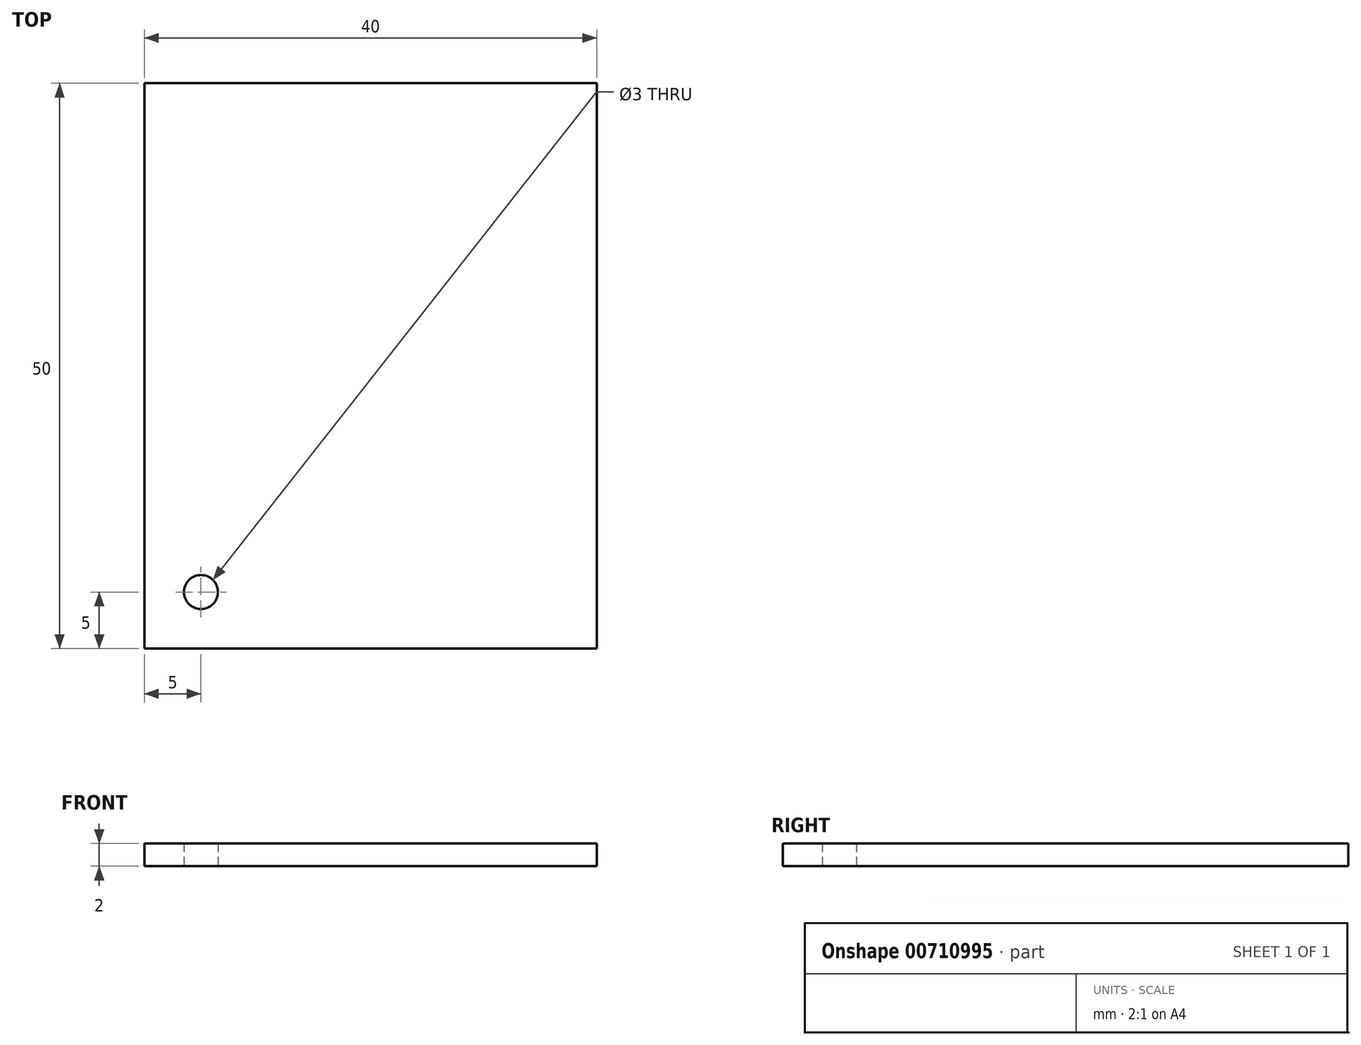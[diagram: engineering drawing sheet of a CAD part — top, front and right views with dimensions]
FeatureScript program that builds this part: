
annotation { "Feature Type Name" : "Feature", "Feature Type Description" : "" }
export const myFeature = defineFeature(function(context is Context, id is Id, definition is map)
    precondition{}
    {
        {
            var Q0;
            Q0=qCreatedBy(makeId("Top.planeOp"),FACE);
            var sketch = newSketch(context, id + "F0", { "sketchPlane" : qUnion([Q0])});
            skLineSegment(sketch, "E0.bottom", {"start": v(0, 0) * mm, "end": v(40, 0) * mm});
            skLineSegment(sketch, "E0.top", {"start": v(0, 50) * mm, "end": v(40, 50) * mm});
            skLineSegment(sketch, "E0.left", {"start": v(0, 0) * mm, "end": v(0, 50) * mm});
            skLineSegment(sketch, "E0.right", {"start": v(40, 0) * mm, "end": v(40, 50) * mm});
            skCircle(sketch, "E1", {"center": v(5, 5) * mm, "radius": 1.5 * mm});
            skSolve(sketch);
        }
        {
            var Q0;
            Q0=makeQuery(id+"F0.imprint","IMPRINT",FACE,{"disambiguationData":[TD([[makeQuery(id+"F0.imprint","IMPRINT",EDGE,{"derivedFrom":sQuery(id+"F0.wireOp",EDGE,"E0.bottom")}),1.0]])]});
            extrude(context, id + "F1", {"entities" : qUnion([Q0]), "depth" : 2 * mm, "offsetDistance" : 25 * mm});
        }
    });
